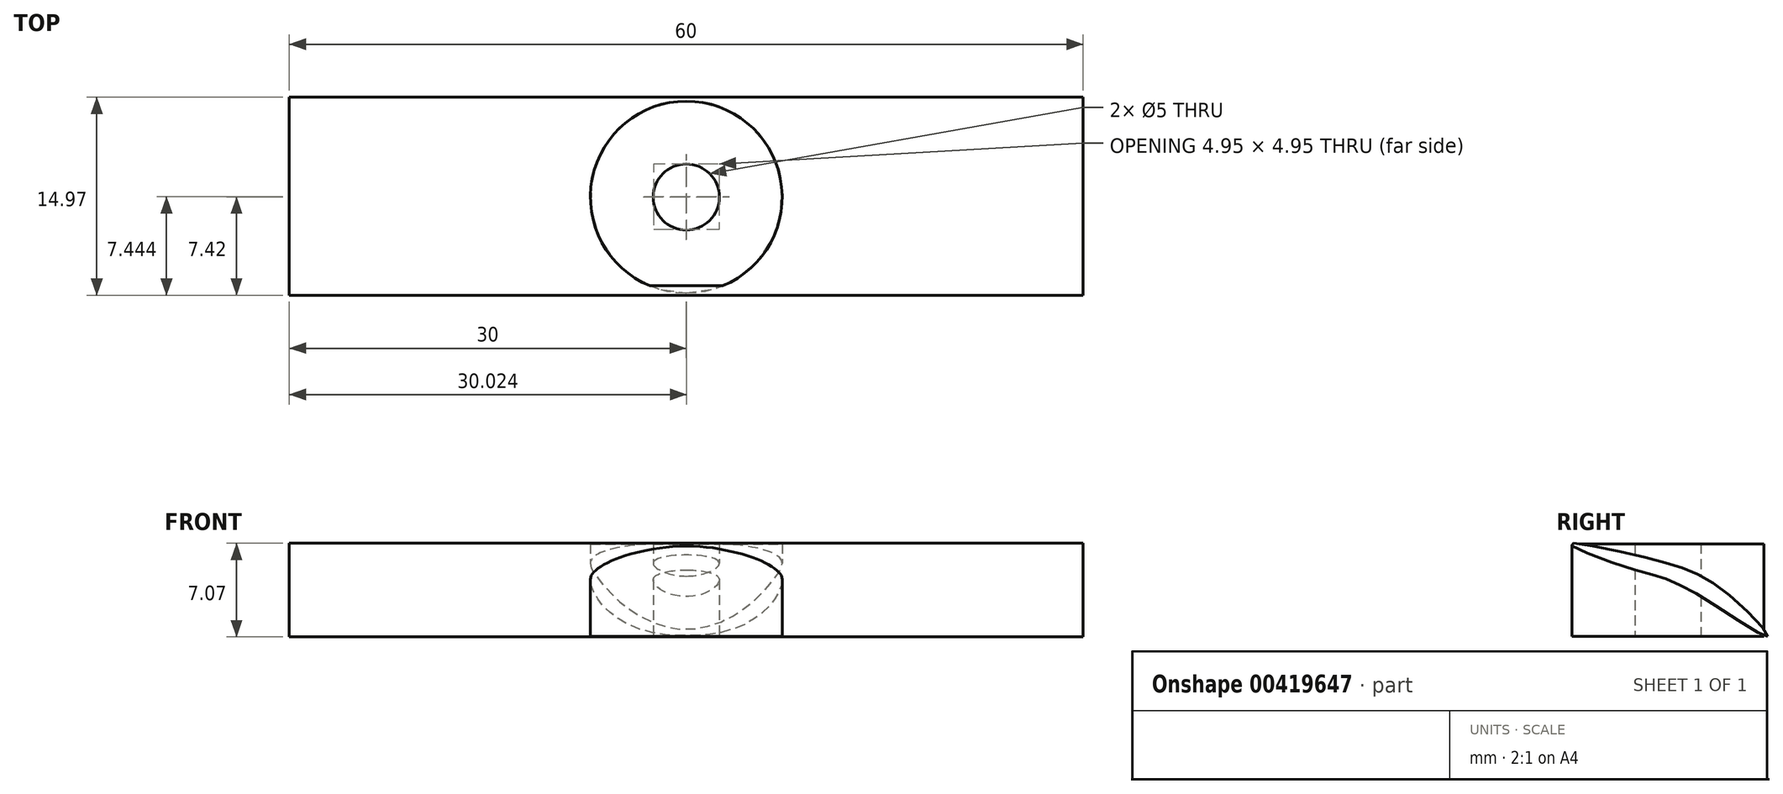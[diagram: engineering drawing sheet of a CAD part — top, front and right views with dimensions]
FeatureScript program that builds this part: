
annotation { "Feature Type Name" : "Feature", "Feature Type Description" : "" }
export const myFeature = defineFeature(function(context is Context, id is Id, definition is map)
    precondition{}
    {
        {
            var Q0;
            Q0=qCreatedBy(makeId("Top.planeOp"),FACE);
            var sketch = newSketch(context, id + "F0", { "sketchPlane" : qUnion([Q0])});
            skCircle(sketch, "E0", {"center": v(0, 0) * mm, "radius": 7.25 * mm});
            skCircle(sketch, "E1", {"center": v(0, 0) * mm, "radius": 2.5 * mm});
            skSolve(sketch);
        }
        {
            var Q0;
            Q0=makeQuery(id+"F0.imprint","IMPRINT",FACE,{"disambiguationData":[TD([[makeQuery(id+"F0.imprint","IMPRINT",EDGE,{"derivedFrom":sQuery(id+"F0.wireOp",EDGE,"E0")}),1.0]])]});
            extrude(context, id + "F1", {"entities" : qUnion([Q0]), "depth" : 7 * mm});
        }
        {
            var Q0;
            Q0=qCreatedBy(makeId("Right.planeOp"),FACE);
            var sketch = newSketch(context, id + "F2", { "sketchPlane" : qUnion([Q0])});
            skFitSpline(sketch, "E2", {"points": [v(7.53, 0) * mm, v(4.97, 2.85) * mm, v(1.61, 4.97) * mm, v(-2.6, 6.18) * mm, v(-7.42, 7) * mm, v(-3.03, 5.2) * mm, v(0, 4.29) * mm, v(3.6, 2.33) * mm, v(7.53, 0) * mm]});
            skSolve(sketch);
        }
        {
            var Q0;
            Q0=makeQuery(id+"F2.imprint","IMPRINT",FACE,{"disambiguationData":[TD([[makeQuery(id+"F2.imprint","IMPRINT",EDGE,{"derivedFrom":sQuery(id+"F2.wireOp",EDGE,"E2")}),1.0]])]});
            var Q1;
            Q1=sQuery(id+"F2.wireOp",EDGE,"E2");
            extrude(context, id + "F3", {"entities" : qUnion([Q0]), "operationType" : NewBodyOperationType.ADD, "surfaceEntities" : qUnion([Q1]), "depth" : 30 * mm});
        }
        {
            var Q0;
            Q0 = qSketchRegion(id + "F2", true);
            extrude(context, id + "F4", {"entities" : qUnion([Q0]), "operationType" : NewBodyOperationType.ADD, "oppositeDirection" : true, "depth" : 30 * mm});
        }
    });
